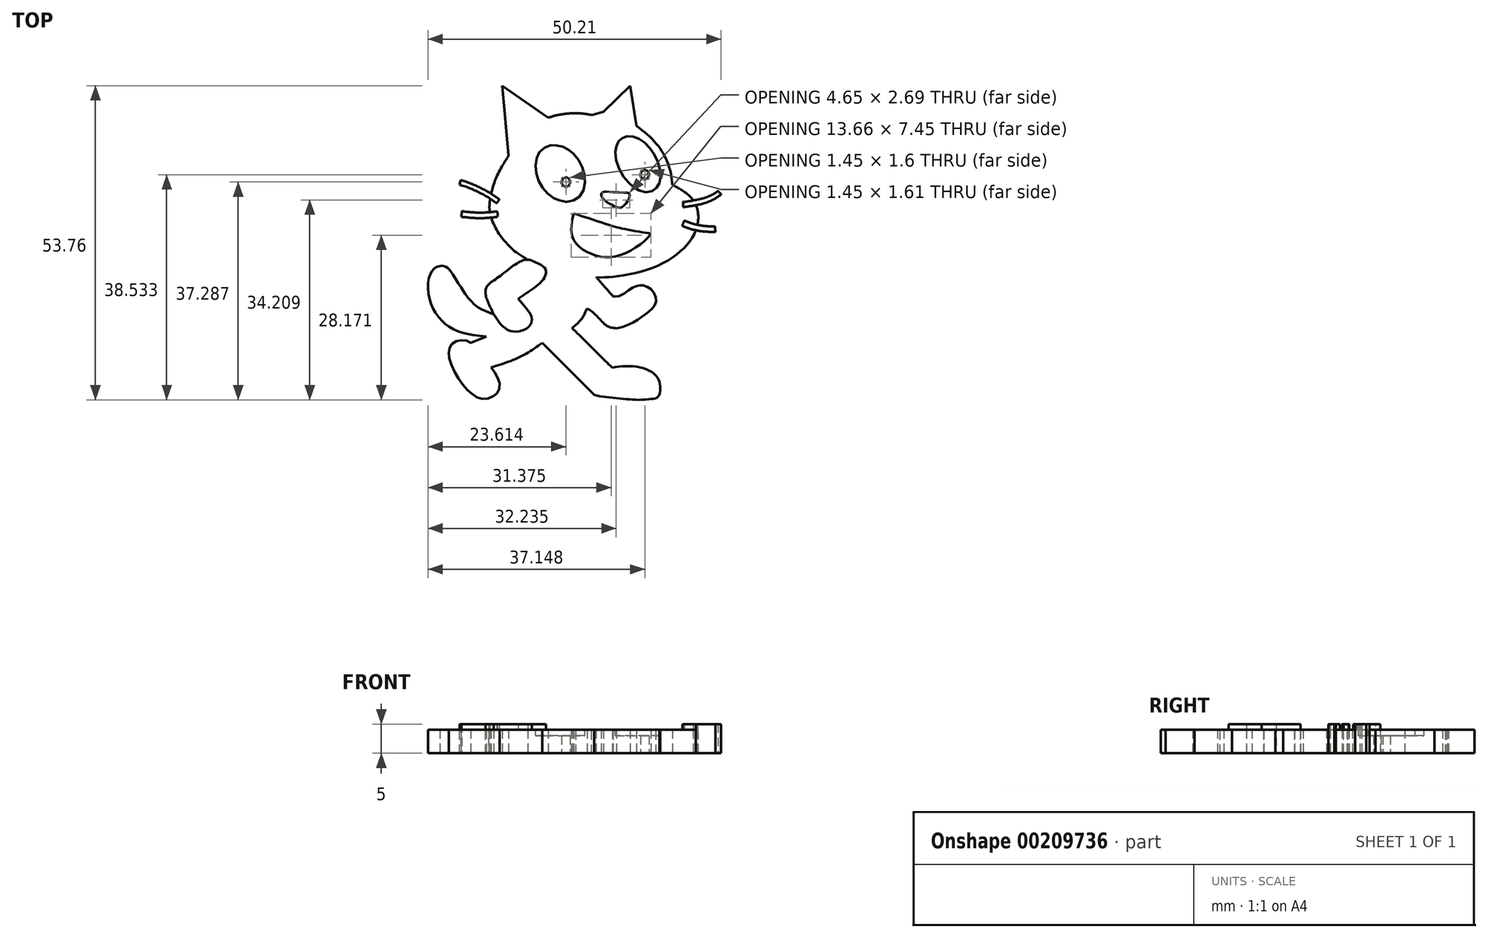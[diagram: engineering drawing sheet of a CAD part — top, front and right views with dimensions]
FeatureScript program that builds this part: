
annotation { "Feature Type Name" : "Feature", "Feature Type Description" : "" }
export const myFeature = defineFeature(function(context is Context, id is Id, definition is map)
    precondition{}
    {
        {
            var Q0;
            Q0=qCreatedBy(makeId("Top.planeOp"),FACE);
            var sketch = newSketch(context, id + "F0", { "sketchPlane" : qUnion([Q0])});
            skPoint(sketch, "E0", {"position": v(-15.53, 54.37) * mm});
            skPoint(sketch, "E1", {"position": v(-37.48, 54.37) * mm});
            skPoint(sketch, "E2", {"position": v(-14.45, 47.5) * mm});
            skPoint(sketch, "E3", {"position": v(-8.3, 37.37) * mm});
            skPoint(sketch, "E4", {"position": v(-20.1, 49.93) * mm});
            skPoint(sketch, "E5", {"position": v(-29.55, 48.9) * mm});
            skPoint(sketch, "E6", {"position": v(-36.34, 42.43) * mm});
            skPoint(sketch, "E7", {"position": v(-33.05, 24.6) * mm});
            skPoint(sketch, "E8", {"position": v(-39.8, 20.36) * mm});
            skPoint(sketch, "E9", {"position": v(-38.9, 15.28) * mm});
            skPoint(sketch, "E10", {"position": v(-34.65, 18.41) * mm});
            skPoint(sketch, "E11", {"position": v(-48.12, 23.53) * mm});
            skPoint(sketch, "E12", {"position": v(-40.17, 11.41) * mm});
            skPoint(sketch, "E13", {"position": v(-39.36, 6.16) * mm});
            skPoint(sketch, "E14", {"position": v(-30.61, 10.34) * mm});
            skPoint(sketch, "E15", {"position": v(-21.72, 1.45) * mm});
            skPoint(sketch, "E16", {"position": v(-10.55, 1.45) * mm});
            skPoint(sketch, "E17", {"position": v(-18.61, 6.13) * mm});
            skPoint(sketch, "E18", {"position": v(-25.5, 12.9) * mm});
            skPoint(sketch, "E19", {"position": v(-22.94, 16.26) * mm});
            skPoint(sketch, "E20", {"position": v(-17.88, 12.85) * mm});
            skPoint(sketch, "E21", {"position": v(-18.45, 18.3) * mm});
            skPoint(sketch, "E22", {"position": v(-21.37, 21.6) * mm});
            skLineSegment(sketch, "E23", {"start": v(-37.48, 54.37) * mm, "end": v(-29.55, 48.9) * mm});
            skLineSegment(sketch, "E24", {"start": v(-37.48, 54.37) * mm, "end": v(-36.34, 42.43) * mm});
            skLineSegment(sketch, "E25", {"start": v(-20.1, 49.93) * mm, "end": v(-15.53, 54.37) * mm});
            skLineSegment(sketch, "E26", {"start": v(-15.53, 54.37) * mm, "end": v(-14.45, 47.5) * mm});
            skFitSpline(sketch, "E27", {"points": [v(-14.45, 47.5) * mm, v(-9.87, 42.79) * mm, v(-8.3, 37.37) * mm], "startDerivative": vector(11.2, -8.29) * mm, "endDerivative": vector(0.98, -11.71) * mm});
            skFitSpline(sketch, "E28", {"points": [v(-8.3, 37.37) * mm, v(-4.62, 34.6) * mm, v(-3.9, 31.3) * mm, v(-4.91, 28.38) * mm, v(-7.43, 25.63) * mm, v(-12.19, 23.04) * mm, v(-18.07, 21.72) * mm, v(-21.37, 21.6) * mm], "startDerivative": vector(29.09, -13.56) * mm, "endDerivative": vector(-26.28, 1.27) * mm});
            skFitSpline(sketch, "E29", {"points": [v(-21.37, 21.6) * mm, v(-20.12, 20.22) * mm, v(-18.45, 18.3) * mm], "startDerivative": vector(3.43, -3.54) * mm, "endDerivative": vector(3.3, -3.62) * mm});
            skFitSpline(sketch, "E30", {"points": [v(-18.45, 18.3) * mm, v(-18.43, 18.3) * mm, v(-17.66, 18.3) * mm, v(-15.6, 19.52) * mm, v(-14.36, 20.13) * mm, v(-13.44, 20.2) * mm, v(-12.19, 19.7) * mm, v(-11.18, 18.3) * mm, v(-11.26, 16.93) * mm, v(-12.28, 15.77) * mm, v(-13.48, 14.87) * mm, v(-15.23, 13.74) * mm, v(-17.88, 12.85) * mm], "startDerivative": vector(11.31, -2.03) * mm, "endDerivative": vector(-26.03, -6.17) * mm});
            skFitSpline(sketch, "E31", {"points": [v(-17.88, 12.85) * mm, v(-19.06, 13.05) * mm, v(-20.34, 13.97) * mm, v(-21.99, 15.66) * mm, v(-22.94, 16.26) * mm], "startDerivative": vector(-5.62, 1.03) * mm, "endDerivative": vector(-3.97, 1.85) * mm});
            skFitSpline(sketch, "E32", {"points": [v(-22.94, 16.26) * mm, v(-23.82, 14.53) * mm, v(-25.5, 12.9) * mm], "startDerivative": vector(-1.54, -3.76) * mm, "endDerivative": vector(-3.55, -2.99) * mm});
            skFitSpline(sketch, "E33", {"points": [v(-25.5, 12.9) * mm, v(-18.61, 6.13) * mm], "startDerivative": vector(6.87, -6.46) * mm, "endDerivative": vector(6.87, -6.46) * mm});
            skFitSpline(sketch, "E34", {"points": [v(-18.61, 6.13) * mm, v(-17.02, 6.37) * mm, v(-15.18, 6.34) * mm, v(-13.56, 6.13) * mm, v(-12.24, 5.59) * mm, v(-11.3, 4.94) * mm, v(-10.67, 4.13) * mm, v(-10.48, 3.5) * mm, v(-10.4, 2.8) * mm, v(-10.43, 2.08) * mm, v(-10.55, 1.45) * mm], "startDerivative": vector(12.84, 2.52) * mm, "endDerivative": vector(-1.77, -8.06) * mm});
            skFitSpline(sketch, "E35", {"points": [v(-10.55, 1.45) * mm, v(-11, 0.97) * mm, v(-11.6, 0.8) * mm, v(-12.62, 0.67) * mm, v(-14.5, 0.62) * mm, v(-16.13, 0.73) * mm, v(-18.15, 0.92) * mm, v(-20.15, 1.13) * mm, v(-21.72, 1.45) * mm], "startDerivative": vector(-4.78, -6.47) * mm, "endDerivative": vector(-11.28, 2.56) * mm});
            skFitSpline(sketch, "E36", {"points": [v(-21.72, 1.45) * mm, v(-30.61, 10.34) * mm], "startDerivative": vector(-8.89, 8.89) * mm, "endDerivative": vector(-8.89, 8.89) * mm});
            skFitSpline(sketch, "E37", {"points": [v(-30.61, 10.34) * mm, v(-34.52, 7.9) * mm, v(-39.36, 6.16) * mm], "startDerivative": vector(-7.7, -5.38) * mm, "endDerivative": vector(-9.78, -3) * mm});
            skFitSpline(sketch, "E38", {"points": [v(-39.36, 6.16) * mm, v(-38.65, 5.15) * mm, v(-38.08, 4.07) * mm, v(-37.9, 3.2) * mm, v(-38.05, 2.2) * mm, v(-38.4, 1.69) * mm, v(-38.87, 1.29) * mm, v(-39.9, 0.86) * mm, v(-41.03, 0.78) * mm, v(-41.92, 1.12) * mm, v(-42.93, 1.84) * mm, v(-43.75, 2.66) * mm, v(-44.82, 4.04) * mm, v(-45.63, 5.45) * mm, v(-46.36, 7.27) * mm, v(-46.6, 8.32) * mm, v(-46.58, 9.1) * mm, v(-46.3, 9.86) * mm, v(-45.9, 10.34) * mm, v(-44.93, 10.76) * mm, v(-44.12, 10.79) * mm, v(-43.47, 10.7) * mm, v(-42.86, 10.34) * mm], "startDerivative": vector(14.44, -19.47) * mm, "endDerivative": vector(15.47, -11.71) * mm});
            skFitSpline(sketch, "E39", {"points": [v(-42.86, 10.34) * mm, v(-40.17, 11.41) * mm], "startDerivative": vector(2.7, 1.08) * mm, "endDerivative": vector(2.7, 1.08) * mm});
            skFitSpline(sketch, "E40", {"points": [v(-40.17, 11.41) * mm, v(-43.2, 11.85) * mm, v(-45.05, 12.37) * mm, v(-46.81, 13.32) * mm, v(-47.95, 14.33) * mm, v(-49.2, 16.02) * mm, v(-49.87, 17.81) * mm, v(-50.17, 20.13) * mm, v(-49.94, 21.7) * mm, v(-49.39, 22.77) * mm, v(-48.83, 23.29) * mm, v(-48.12, 23.53) * mm], "startDerivative": vector(-26.3, 3.36) * mm, "endDerivative": vector(12.38, 3.1) * mm});
            skFitSpline(sketch, "E41", {"points": [v(-48.12, 23.53) * mm, v(-47.53, 23.53) * mm, v(-46.81, 23.22) * mm, v(-46.2, 22.5) * mm, v(-44.2, 19.36) * mm, v(-43.39, 18.2) * mm, v(-42.6, 17.33) * mm, v(-41.53, 16.42) * mm, v(-38.9, 15.28) * mm], "startDerivative": vector(6.83, 0.7) * mm, "endDerivative": vector(15.96, -5.18) * mm});
            skFitSpline(sketch, "E42", {"points": [v(-38.9, 15.28) * mm, v(-39.86, 17.29) * mm, v(-40.27, 18.48) * mm, v(-40.33, 19.24) * mm, v(-40.18, 19.84) * mm, v(-39.8, 20.36) * mm], "startDerivative": vector(-4.13, 8) * mm, "endDerivative": vector(3.47, 3) * mm});
            skFitSpline(sketch, "E43", {"points": [v(-39.8, 20.36) * mm, v(-39.28, 20.8) * mm, v(-38.8, 21.12) * mm, v(-37.98, 21.7) * mm, v(-37.17, 22.31) * mm, v(-35.7, 23.48) * mm, v(-34.77, 24.06) * mm, v(-34.12, 24.39) * mm, v(-33.54, 24.58) * mm, v(-33.05, 24.6) * mm], "startDerivative": vector(5.63, 5.66) * mm, "endDerivative": vector(6.01, -0.05) * mm});
            skFitSpline(sketch, "E44", {"points": [v(-33.05, 24.6) * mm, v(-35.07, 25.86) * mm, v(-36.37, 27.07) * mm, v(-37.95, 28.95) * mm, v(-38.78, 30.46) * mm, v(-39.44, 32.02) * mm, v(-39.63, 34.12) * mm, v(-39.22, 36.44) * mm, v(-38.42, 38.77) * mm, v(-37.27, 40.97) * mm, v(-36.34, 42.43) * mm], "startDerivative": vector(-20.86, 13.04) * mm, "endDerivative": vector(10.37, 15.6) * mm});
            skFitSpline(sketch, "E45", {"points": [v(-29.55, 48.9) * mm, v(-28.03, 49.35) * mm, v(-26.15, 49.62) * mm, v(-24.57, 49.68) * mm, v(-23.05, 49.53) * mm, v(-22.15, 49.38) * mm], "startDerivative": vector(7.05, 2.38) * mm, "endDerivative": vector(5.3, -0.95) * mm});
            skFitSpline(sketch, "E46", {"points": [v(-22.15, 49.38) * mm, v(-20.1, 49.93) * mm], "startDerivative": vector(2.05, 0.55) * mm, "endDerivative": vector(2.05, 0.55) * mm});
            skFitSpline(sketch, "E47", {"points": [v(-30.23, 43.79) * mm, v(-29.26, 44.18) * mm, v(-28.48, 44.18) * mm, v(-27.6, 44.13) * mm, v(-26.83, 43.84) * mm, v(-25.96, 43.35) * mm, v(-25.18, 42.67) * mm, v(-24.2, 41.46) * mm, v(-23.62, 40.05) * mm, v(-23.28, 38.59) * mm, v(-23.33, 37.33) * mm, v(-23.77, 35.96) * mm, v(-24.6, 35.09) * mm, v(-25.66, 34.6) * mm, v(-26.78, 34.5) * mm, v(-27.85, 34.8) * mm, v(-28.73, 35.19) * mm, v(-29.8, 36.01) * mm, v(-30.62, 37.03) * mm, v(-31.3, 38.4) * mm, v(-31.7, 39.7) * mm, v(-31.74, 41.07) * mm, v(-31.45, 42.23) * mm, v(-31.01, 43.1) * mm, v(-30.23, 43.79) * mm]});
            skFitSpline(sketch, "E48", {"points": [v(-26.56, 38.7) * mm, v(-26.18, 38.59) * mm, v(-25.95, 38.3) * mm, v(-25.83, 37.94) * mm, v(-25.9, 37.53) * mm, v(-26.17, 37.23) * mm, v(-26.51, 37.1) * mm, v(-26.99, 37.26) * mm, v(-27.25, 37.64) * mm, v(-27.27, 38.05) * mm, v(-27.15, 38.38) * mm, v(-26.92, 38.57) * mm, v(-26.56, 38.7) * mm]});
            skFitSpline(sketch, "E49", {"points": [v(-16.08, 45.7) * mm, v(-15.3, 45.7) * mm, v(-14.65, 45.55) * mm, v(-13.79, 45.15) * mm, v(-13.04, 44.6) * mm, v(-12.25, 43.77) * mm, v(-11.48, 42.75) * mm, v(-10.92, 41.64) * mm, v(-10.52, 40.38) * mm, v(-10.34, 39.31) * mm, v(-10.43, 38.16) * mm, v(-10.65, 37.48) * mm, v(-10.96, 36.96) * mm, v(-11.38, 36.54) * mm, v(-12.06, 36.24) * mm, v(-12.96, 36.16) * mm, v(-13.91, 36.43) * mm, v(-14.69, 36.84) * mm, v(-15.43, 37.43) * mm, v(-16.04, 38.04) * mm, v(-16.93, 39.18) * mm, v(-17.67, 40.8) * mm, v(-18.04, 42.32) * mm, v(-18.04, 43.37) * mm, v(-17.89, 44.01) * mm, v(-17.64, 44.63) * mm, v(-17.33, 45.1) * mm, v(-16.96, 45.37) * mm, v(-16.53, 45.58) * mm, v(-16.08, 45.7) * mm]});
            skFitSpline(sketch, "E50", {"points": [v(-12.96, 39.95) * mm, v(-12.71, 39.88) * mm, v(-12.42, 39.63) * mm, v(-12.3, 39.31) * mm, v(-12.37, 38.8) * mm, v(-12.6, 38.52) * mm, v(-12.96, 38.34) * mm, v(-13.42, 38.47) * mm, v(-13.7, 38.84) * mm, v(-13.74, 39.31) * mm, v(-13.6, 39.64) * mm, v(-13.33, 39.88) * mm, v(-12.96, 39.95) * mm]});
            skFitSpline(sketch, "E51", {"points": [v(-20.26, 36.16) * mm, v(-19.8, 36.25) * mm, v(-19.24, 36.22) * mm, v(-18.4, 36.16) * mm, v(-17.17, 36.12) * mm, v(-16.32, 36.08) * mm, v(-15.96, 36.04) * mm, v(-15.77, 35.96) * mm, v(-15.64, 35.85) * mm, v(-15.58, 35.66) * mm, v(-15.62, 35.41) * mm, v(-15.8, 35) * mm, v(-16.16, 34.4) * mm, v(-16.42, 34.03) * mm, v(-16.71, 33.75) * mm, v(-16.96, 33.59) * mm, v(-17.16, 33.5) * mm, v(-17.36, 33.47) * mm, v(-17.66, 33.53) * mm, v(-18.2, 33.72) * mm, v(-18.68, 33.97) * mm, v(-19.35, 34.37) * mm, v(-19.7, 34.63) * mm, v(-20.08, 34.97) * mm, v(-20.4, 35.35) * mm, v(-20.48, 35.6) * mm, v(-20.48, 35.87) * mm, v(-20.4, 36.04) * mm, v(-20.26, 36.16) * mm]});
            skFitSpline(sketch, "E52", {"points": [v(-33.05, 24.6) * mm, v(-32.77, 24.58) * mm, v(-32.5, 24.5) * mm, v(-32.17, 24.38) * mm, v(-31.67, 24.13) * mm, v(-30.86, 23.73) * mm, v(-30.47, 23.46) * mm, v(-30.2, 23.21) * mm, v(-30.03, 22.94) * mm, v(-29.95, 22.54) * mm, v(-29.98, 22.17) * mm, v(-30.1, 21.76) * mm, v(-30.33, 21.34) * mm, v(-30.63, 20.98) * mm, v(-31.01, 20.6) * mm, v(-31.38, 20.25) * mm, v(-31.89, 19.86) * mm, v(-32.37, 19.5) * mm, v(-34.71, 17.9) * mm], "startDerivative": vector(6.74, -0.41) * mm, "endDerivative": vector(-21.93, -14.97) * mm});
            skFitSpline(sketch, "E53", {"points": [v(-34.71, 17.9) * mm, v(-33.45, 16.44) * mm, v(-32.9, 15.74) * mm, v(-32.6, 15.24) * mm, v(-32.47, 14.84) * mm, v(-32.37, 14.54) * mm, v(-32.37, 14.08) * mm, v(-32.5, 13.65) * mm, v(-32.7, 13.33) * mm, v(-33.03, 13.02) * mm, v(-33.35, 12.8) * mm, v(-34.01, 12.5) * mm, v(-34.8, 12.3) * mm, v(-35.2, 12.28) * mm, v(-35.61, 12.3) * mm, v(-36.04, 12.4) * mm, v(-36.45, 12.55) * mm, v(-36.81, 12.77) * mm, v(-37.25, 13.08) * mm, v(-37.59, 13.4) * mm, v(-37.91, 13.78) * mm, v(-38.2, 14.2) * mm, v(-38.4, 14.48) * mm, v(-38.62, 14.82) * mm, v(-38.9, 15.28) * mm], "startDerivative": vector(17.58, -20.04) * mm, "endDerivative": vector(-5.85, 10) * mm});
            skFitSpline(sketch, "E54", {"points": [v(-25.17, 32.5) * mm, v(-23.04, 31.82) * mm, v(-20.46, 31) * mm, v(-18.47, 30.35) * mm, v(-17.55, 30.1) * mm, v(-16.67, 29.88) * mm, v(-14.8, 29.52) * mm, v(-13.2, 29.26) * mm, v(-11.97, 29.05) * mm], "startDerivative": vector(14.21, -4.6) * mm, "endDerivative": vector(11.07, -1.97) * mm});
            skFitSpline(sketch, "E55", {"points": [v(-11.97, 29.05) * mm, v(-12.49, 28.39) * mm, v(-13.24, 27.68) * mm, v(-14, 27.09) * mm, v(-14.9, 26.5) * mm, v(-15.82, 25.95) * mm, v(-16.89, 25.5) * mm, v(-17.9, 25.2) * mm, v(-18.9, 25.03) * mm, v(-19.8, 25) * mm, v(-20.53, 25.1) * mm, v(-21.2, 25.27) * mm, v(-22.04, 25.53) * mm, v(-22.7, 25.86) * mm, v(-23.44, 26.24) * mm, v(-23.94, 26.57) * mm, v(-24.55, 27.09) * mm, v(-24.98, 27.63) * mm, v(-25.36, 28.34) * mm, v(-25.6, 29.31) * mm, v(-25.62, 30.14) * mm, v(-25.47, 31.37) * mm, v(-25.17, 32.5) * mm], "startDerivative": vector(-10.94, -15.13) * mm, "endDerivative": vector(6.63, 21.24) * mm});
            skPoint(sketch, "E56", {"position": v(-4.73, 34.75) * mm});
            skPoint(sketch, "E57", {"position": v(-4.27, 33.93) * mm});
            skPoint(sketch, "E58", {"position": v(-0.52, 36.4) * mm});
            skPoint(sketch, "E59", {"position": v(0.04, 35.8) * mm});
            skPoint(sketch, "E60", {"position": v(-4.02, 30.58) * mm});
            skPoint(sketch, "E61", {"position": v(-4.29, 29.66) * mm});
            skPoint(sketch, "E62", {"position": v(-0.97, 29.36) * mm});
            skPoint(sketch, "E63", {"position": v(-0.99, 30.32) * mm});
            skFitSpline(sketch, "E64", {"points": [v(-4.73, 34.75) * mm, v(-3.88, 34.9) * mm, v(-3.35, 35.03) * mm, v(-2.77, 35.2) * mm, v(-2.03, 35.47) * mm, v(-1.42, 35.77) * mm, v(-0.99, 36.03) * mm, v(-0.52, 36.4) * mm], "startDerivative": vector(4.98, 0.94) * mm, "endDerivative": vector(3.43, 2.84) * mm});
            skFitSpline(sketch, "E65", {"points": [v(-0.52, 36.4) * mm, v(0.04, 35.8) * mm], "startDerivative": vector(0.25, -0.33) * mm, "endDerivative": vector(0.25, -0.33) * mm});
            skFitSpline(sketch, "E66", {"points": [v(0.04, 35.8) * mm, v(-0.42, 35.45) * mm, v(-0.6, 35.33) * mm, v(-0.83, 35.18) * mm, v(-1.07, 35.03) * mm, v(-1.43, 34.84) * mm, v(-1.77, 34.67) * mm, v(-2.26, 34.47) * mm, v(-2.82, 34.27) * mm, v(-3.25, 34.16) * mm, v(-3.74, 34.05) * mm, v(-4.27, 33.93) * mm], "startDerivative": vector(-2.97, -2.02) * mm, "endDerivative": vector(-5.72, -0.82) * mm});
            skFitSpline(sketch, "E67", {"points": [v(-4.02, 30.58) * mm, v(-3.85, 30.55) * mm, v(-3.65, 30.5) * mm, v(-3.37, 30.45) * mm, v(-3.1, 30.42) * mm, v(-2.77, 30.37) * mm, v(-2.45, 30.35) * mm, v(-2.03, 30.32) * mm, v(-1.69, 30.3) * mm, v(-1.3, 30.31) * mm, v(-0.99, 30.32) * mm], "startDerivative": vector(2.18, -0.52) * mm, "endDerivative": vector(3, 0.13) * mm});
            skFitSpline(sketch, "E68", {"points": [v(-0.99, 30.32) * mm, v(-0.97, 29.36) * mm], "startDerivative": vector(0, -0.44) * mm, "endDerivative": vector(0, -0.44) * mm});
            skFitSpline(sketch, "E69", {"points": [v(-0.97, 29.36) * mm, v(-1.32, 29.36) * mm, v(-1.68, 29.36) * mm, v(-2.01, 29.37) * mm, v(-2.36, 29.39) * mm, v(-2.72, 29.42) * mm, v(-3.04, 29.44) * mm, v(-3.37, 29.47) * mm, v(-3.7, 29.51) * mm, v(-3.96, 29.57) * mm, v(-4.29, 29.66) * mm], "startDerivative": vector(-2.75, 0) * mm, "endDerivative": vector(-2.62, 0.4) * mm});
            skPoint(sketch, "E70", {"position": v(-44.57, 38.25) * mm});
            skPoint(sketch, "E71", {"position": v(-44.77, 37.44) * mm});
            skPoint(sketch, "E72", {"position": v(-39.35, 35.9) * mm});
            skPoint(sketch, "E73", {"position": v(-39.52, 35.07) * mm});
            skPoint(sketch, "E74", {"position": v(-39.59, 32.73) * mm});
            skPoint(sketch, "E75", {"position": v(-39.38, 31.82) * mm});
            skPoint(sketch, "E76", {"position": v(-44.34, 32.92) * mm});
            skPoint(sketch, "E77", {"position": v(-44.41, 31.96) * mm});
            skFitSpline(sketch, "E78", {"points": [v(-44.57, 38.25) * mm, v(-44.77, 37.44) * mm], "startDerivative": vector(-0.12, -0.43) * mm, "endDerivative": vector(-0.12, -0.43) * mm});
            skFitSpline(sketch, "E79", {"points": [v(-44.57, 38.25) * mm, v(-44.25, 38.16) * mm, v(-43.86, 38.02) * mm, v(-43.5, 37.9) * mm, v(-43.03, 37.72) * mm, v(-42.52, 37.51) * mm, v(-42.05, 37.3) * mm, v(-41.6, 37.1) * mm, v(-41.16, 36.89) * mm, v(-40.79, 36.7) * mm, v(-40.36, 36.47) * mm, v(-39.99, 36.26) * mm, v(-39.35, 35.9) * mm], "startDerivative": vector(4.5, -1.32) * mm, "endDerivative": vector(6.46, -4.28) * mm});
            skFitSpline(sketch, "E80", {"points": [v(-44.77, 37.44) * mm, v(-44.4, 37.34) * mm, v(-44, 37.21) * mm, v(-43.5, 37.03) * mm, v(-43.04, 36.85) * mm, v(-42.57, 36.66) * mm, v(-42.05, 36.43) * mm, v(-41.56, 36.2) * mm, v(-41.12, 35.98) * mm, v(-40.63, 35.72) * mm, v(-40.16, 35.45) * mm, v(-39.85, 35.26) * mm, v(-39.52, 35.07) * mm], "startDerivative": vector(4.43, -1.67) * mm, "endDerivative": vector(5.1, -3.96) * mm});
            skFitSpline(sketch, "E81", {"points": [v(-44.34, 32.92) * mm, v(-44.41, 31.96) * mm], "startDerivative": vector(-0.04, -0.43) * mm, "endDerivative": vector(-0.04, -0.43) * mm});
            skFitSpline(sketch, "E82", {"points": [v(-44.34, 32.92) * mm, v(-44, 32.85) * mm, v(-43.4, 32.78) * mm, v(-42.7, 32.72) * mm, v(-42.07, 32.68) * mm, v(-41.47, 32.66) * mm, v(-40.89, 32.66) * mm, v(-40.33, 32.7) * mm, v(-39.8, 32.73) * mm, v(-39.59, 32.73) * mm], "startDerivative": vector(3.56, -1.01) * mm, "endDerivative": vector(5.53, 0.52) * mm});
            skFitSpline(sketch, "E83", {"points": [v(-44.41, 31.96) * mm, v(-44.01, 31.9) * mm, v(-43.5, 31.84) * mm, v(-42.77, 31.78) * mm, v(-42.12, 31.73) * mm, v(-41.5, 31.7) * mm, v(-40.85, 31.7) * mm, v(-40.25, 31.74) * mm, v(-39.75, 31.78) * mm, v(-39.38, 31.82) * mm], "startDerivative": vector(4.54, -0.97) * mm, "endDerivative": vector(4.16, 0.43) * mm});
            skCircle(sketch, "E84", {"center": v(-25.08, 50.94) * mm, "radius": 1.28 * mm});
            skCircle(sketch, "E85", {"center": v(-25.08, 50.94) * mm, "radius": 2.03 * mm});
            skFitSpline(sketch, "E86", {"points": [v(-4.73, 34.75) * mm, v(-5.23, 34.65) * mm, v(-5.87, 34.55) * mm, v(-6.5, 34.47) * mm], "startDerivative": vector(-1.83, -0.55) * mm, "endDerivative": vector(-1.92, -0.2) * mm});
            skFitSpline(sketch, "E87", {"points": [v(-6.44, 33.6) * mm, v(-5.8, 33.68) * mm, v(-5.1, 33.8) * mm, v(-4.27, 33.93) * mm], "startDerivative": vector(2, 0.26) * mm, "endDerivative": vector(2.05, 0.55) * mm});
            skFitSpline(sketch, "E88", {"points": [v(-4.02, 30.58) * mm, v(-4.57, 30.7) * mm, v(-5.34, 30.93) * mm, v(-6.27, 31.29) * mm], "startDerivative": vector(-1.9, 0.33) * mm, "endDerivative": vector(-2.5, 0.99) * mm});
            skFitSpline(sketch, "E89", {"points": [v(-6.27, 31.29) * mm, v(-6.62, 30.4) * mm], "startDerivative": vector(-0.18, -0.41) * mm, "endDerivative": vector(-0.18, -0.41) * mm});
            skFitSpline(sketch, "E90", {"points": [v(-6.62, 30.4) * mm, v(-5.93, 30.12) * mm, v(-5.39, 29.93) * mm, v(-4.73, 29.74) * mm, v(-4.29, 29.66) * mm], "startDerivative": vector(2.3, -0.93) * mm, "endDerivative": vector(2.2, -0.5) * mm});
            skFitSpline(sketch, "E91", {"points": [v(-6.5, 34.47) * mm, v(-6.47, 34.23) * mm, v(-6.44, 33.6) * mm], "startDerivative": vector(0, -0.46) * mm, "endDerivative": vector(0, -0.49) * mm});
            skFitSpline(sketch, "E92", {"points": [v(-39.35, 35.9) * mm, v(-39.07, 35.7) * mm, v(-38.7, 35.46) * mm, v(-38.36, 35.23) * mm, v(-37.94, 34.93) * mm], "startDerivative": vector(1.27, -0.84) * mm, "endDerivative": vector(1.58, -1.14) * mm});
            skFitSpline(sketch, "E93", {"points": [v(-37.94, 34.93) * mm, v(-38.06, 34.77) * mm, v(-38.41, 34.26) * mm], "startDerivative": vector(-0.25, -0.34) * mm, "endDerivative": vector(-0.32, -0.4) * mm});
            skFitSpline(sketch, "E94", {"points": [v(-38.41, 34.26) * mm, v(-38.65, 34.44) * mm, v(-38.94, 34.64) * mm, v(-39.3, 34.9) * mm, v(-39.52, 35.07) * mm], "startDerivative": vector(-1.2, 0.9) * mm, "endDerivative": vector(-1.15, 0.7) * mm});
            skFitSpline(sketch, "E95", {"points": [v(-39.59, 32.73) * mm, v(-39.05, 32.8) * mm, v(-38.6, 32.83) * mm, v(-38.26, 32.86) * mm], "startDerivative": vector(1.84, 0.18) * mm, "endDerivative": vector(1.13, 0.1) * mm});
            skFitSpline(sketch, "E96", {"points": [v(-38.26, 32.86) * mm, v(-38.24, 32.26) * mm, v(-38.26, 31.94) * mm], "startDerivative": vector(0, -0.6) * mm, "endDerivative": vector(0, -0.46) * mm});
            skFitSpline(sketch, "E97", {"points": [v(-38.26, 31.94) * mm, v(-38.63, 31.88) * mm, v(-39.06, 31.85) * mm, v(-39.38, 31.82) * mm], "startDerivative": vector(-1.14, -0.1) * mm, "endDerivative": vector(-0.95, -0.1) * mm});
            skSolve(sketch);
        }
        {
            var Q0;
            {var subQ0=sQuery(id+"F0.wireOp",EDGE,"E85");var subQ1=sQuery(id+"F0.wireOp",EDGE,"E45");var subQ2=makeQuery(id+"F0.imprint","INTERSECT",VERTEX,{"disambiguationData":[OD(0.0)],"derivedFrom":[subQ1,subQ0]});Q0=makeQuery(id+"F0.imprint","IMPRINT",FACE,{"disambiguationData":[TD([[makeQuery(id+"F0.imprint","IMPRINT",EDGE,{"disambiguationData":[TD([[subQ2,-1.0]])],"derivedFrom":subQ1}),-1.0]])]});}
            var Q1;
            {var subQ5=sQuery(id+"F0.wireOp",EDGE,"E23");Q1=makeQuery(id+"F0.imprint","IMPRINT",FACE,{"disambiguationData":[TD([[makeQuery(id+"F0.imprint","IMPRINT",EDGE,{"derivedFrom":subQ5}),-1.0]])]});}
            var Q2;
            {var subQ0=sQuery(id+"F0.wireOp",EDGE,"E85");var subQ1=sQuery(id+"F0.wireOp",EDGE,"E45");var subQ2=makeQuery(id+"F0.imprint","INTERSECT",VERTEX,{"disambiguationData":[OD(0.0)],"derivedFrom":[subQ1,subQ0]});Q2=makeQuery(id+"F0.imprint","IMPRINT",FACE,{"disambiguationData":[TD([[makeQuery(id+"F0.imprint","IMPRINT",EDGE,{"disambiguationData":[TD([[subQ2,-1.0]])],"derivedFrom":subQ1}),-1.0]])]});}
            extrude(context, id + "F1", {"entities" : qUnion([Q0, Q1, Q2]), "depth" : 4 * mm});
        }
        {
            var Q0;
            Q0=makeQuery(id+"F0.imprint","IMPRINT",FACE,{"disambiguationData":[TD([[makeQuery(id+"F0.imprint","IMPRINT",EDGE,{"derivedFrom":sQuery(id+"F0.wireOp",EDGE,"E47")}),-1.0]])]});
            var Q1;
            Q1=makeQuery(id+"F0.imprint","IMPRINT",FACE,{"disambiguationData":[TD([[makeQuery(id+"F0.imprint","IMPRINT",EDGE,{"derivedFrom":sQuery(id+"F0.wireOp",EDGE,"E49")}),-1.0]])]});
            extrude(context, id + "F2", {"entities" : qUnion([Q0, Q1]), "operationType" : NewBodyOperationType.ADD, "depth" : 3 * mm});
        }
        {
            var Q0;
            Q0=makeQuery(id+"F0.imprint","IMPRINT",FACE,{"disambiguationData":[TD([[makeQuery(id+"F0.imprint","IMPRINT",EDGE,{"derivedFrom":sQuery(id+"F0.wireOp",EDGE,"E42")}),-1.0]])]});
            var Q1;
            Q1=makeQuery(id+"F0.imprint","IMPRINT",FACE,{"disambiguationData":[TD([[makeQuery(id+"F0.imprint","IMPRINT",EDGE,{"derivedFrom":sQuery(id+"F0.wireOp",EDGE,"E78")}),1.0]])]});
            var Q2;
            {var subQ0=sQuery(id+"F0.wireOp",EDGE,"E92");Q2=makeQuery(id+"F0.imprint","IMPRINT",FACE,{"disambiguationData":[TD([[makeQuery(id+"F0.imprint","IMPRINT",EDGE,{"derivedFrom":subQ0}),-1.0]])]});}
            var Q3;
            Q3=makeQuery(id+"F0.imprint","IMPRINT",FACE,{"disambiguationData":[TD([[makeQuery(id+"F0.imprint","IMPRINT",EDGE,{"derivedFrom":sQuery(id+"F0.wireOp",EDGE,"E81")}),1.0]])]});
            var Q4;
            {var subQ0=sQuery(id+"F0.wireOp",EDGE,"E95");Q4=makeQuery(id+"F0.imprint","IMPRINT",FACE,{"disambiguationData":[TD([[makeQuery(id+"F0.imprint","IMPRINT",EDGE,{"derivedFrom":subQ0}),-1.0]])]});}
            var Q5;
            {var subQ0=sQuery(id+"F0.wireOp",EDGE,"E88");Q5=makeQuery(id+"F0.imprint","IMPRINT",FACE,{"disambiguationData":[TD([[makeQuery(id+"F0.imprint","IMPRINT",EDGE,{"derivedFrom":subQ0}),1.0]])]});}
            var Q6;
            {var subQ0=sQuery(id+"F0.wireOp",EDGE,"E67");Q6=makeQuery(id+"F0.imprint","IMPRINT",FACE,{"disambiguationData":[TD([[makeQuery(id+"F0.imprint","IMPRINT",EDGE,{"derivedFrom":subQ0}),-1.0]])]});}
            var Q7;
            {var subQ0=sQuery(id+"F0.wireOp",EDGE,"E64");Q7=makeQuery(id+"F0.imprint","IMPRINT",FACE,{"disambiguationData":[TD([[makeQuery(id+"F0.imprint","IMPRINT",EDGE,{"derivedFrom":subQ0}),-1.0]])]});}
            var Q8;
            {var subQ0=sQuery(id+"F0.wireOp",EDGE,"E86");Q8=makeQuery(id+"F0.imprint","IMPRINT",FACE,{"disambiguationData":[TD([[makeQuery(id+"F0.imprint","IMPRINT",EDGE,{"derivedFrom":subQ0}),1.0]])]});}
            extrude(context, id + "F3", {"entities" : qUnion([Q0, Q1, Q2, Q3, Q4, Q5, Q6, Q7, Q8]), "operationType" : NewBodyOperationType.ADD, "depth" : 5 * mm});
        }
    });
